# Revit family: Электронная проходная PERCo_KT05.9, КТC01.9A
name_source: partatom
category: Оборудование
units: mm (PartAtom-declared; Revit-internal decimal feet)

## family parameters
Всегда вертикально = Нет
Классификация = Нет
На основе рабочей плоскости = Нет
Общий = Нет
При загрузке вырезать с полостями = Нет
Размер круглого соединителя = Использовать диаметр
Тип детали = Нормальный
Точка расчета площади = Нет

## types (2) — shared parameters
ADSK_URL страницы изделия = https://www.perco.ru
ADSK_Единица измерения = шт.
ADSK_Завод-изготовитель = PERCo
ADSK_Количество = 1
ADSK_Материал наименование = Корпус турникета выполнен из высококачественной нержавеющей стали со вставками из АБС-пластика, планки из нержавеющей стали
ADSK_Напряжение = 12 В
ADSK_Номинальная мощность = 72 Вт
ADSK_Ток = 6 А
Габаритные размеры (длина×ширина×высота) = 1170×750×1030 мм
Длина планки = 567 мм
Корпус = PERCo_Нержавейка
Наличие сканеров отпечатка пальцев = Нет
Наличие сканеров штрих-кода = Нет
Панель = PERCo_Пластик черный
Подключение к электросети = 220 В
Пропускная способность = 30 чел./мин
Степень защиты оболочки = IP41
Температура использования = от +1°С до +50°С
Тип контроллера = CT03.2
Тип планки "Антипаника" = Автоматическая
Формат читаемых карт = Mifare, EMM, HID Prox
Ширина зоны прохода = 560 мм.

## per-type parameters (varying)
| type | ADSK_Масса_Текст | ADSK_Наименование | ADSK_Наименование краткое | Емкость картоприёмника | Картоприёмник |
| КТ05.9A | не более 67 кг | Электронная проходная PERCo-KT05.9А с планками Антипаника, для карт EMM/HID, карт Mifare стандарта ISO 14443 с опцией защиты от копирования, смартфонов | Электронная проходная KT05.9А | Не предусмотрено | Нет |
| КТC01.9A | не более 68 кг | Электронная проходная PERCo-KTC01.9А со встроенным картоприемником, планками Антипаника, для карт EMM/HID, карт Mifare стандарта ISO 14443 с опцией защиты от копирования, смартфонов | Электронная проходная KTC01.9A | 350 карт | Да |
